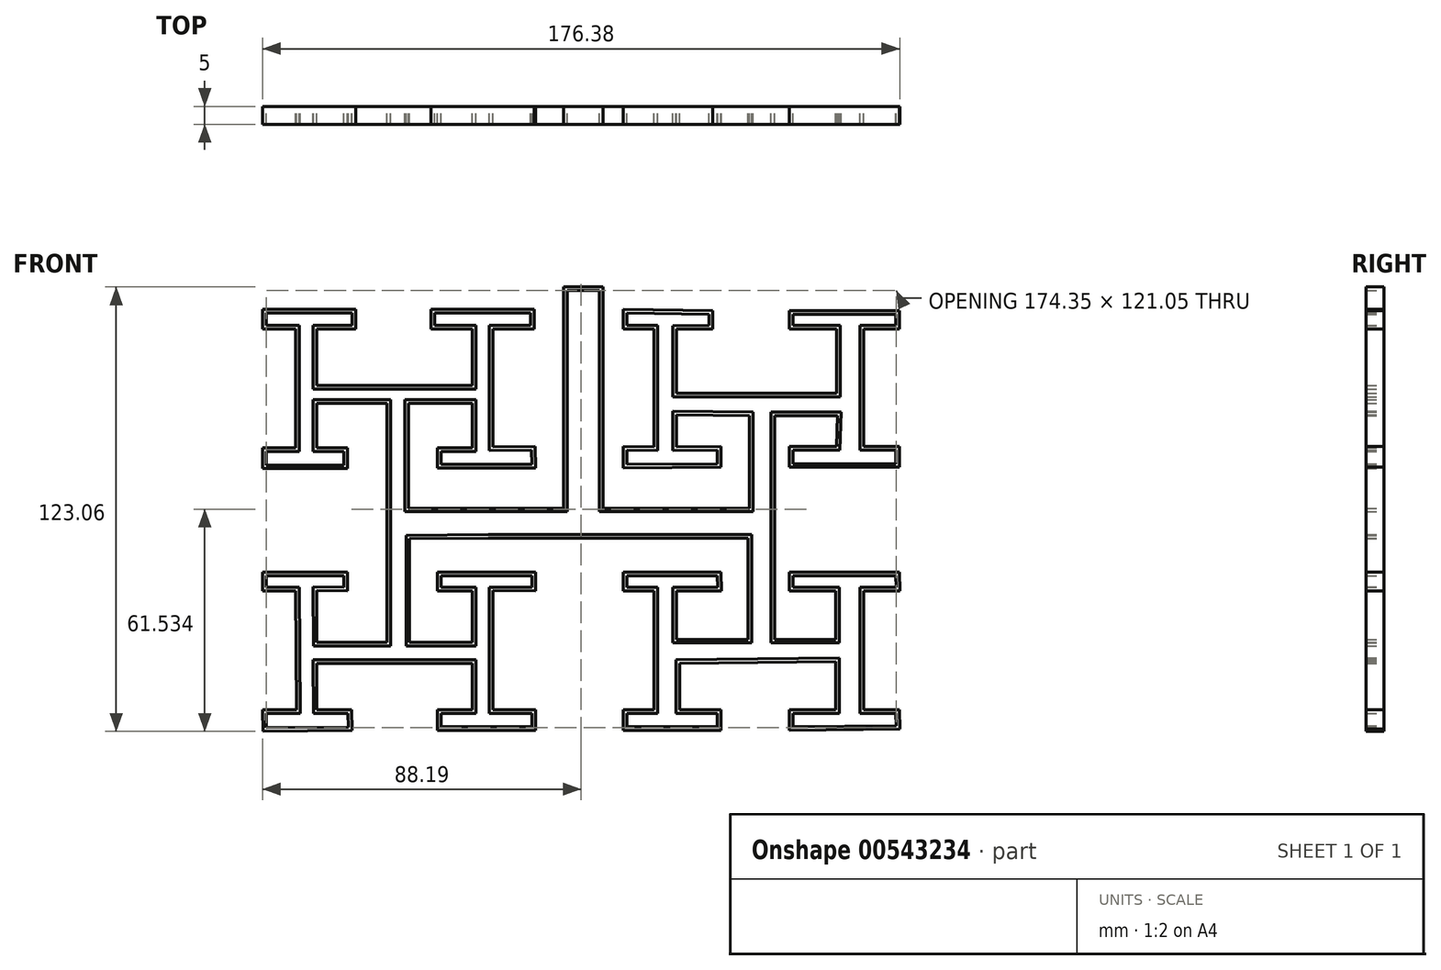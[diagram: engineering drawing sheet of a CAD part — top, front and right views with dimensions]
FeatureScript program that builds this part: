
annotation { "Feature Type Name" : "Feature", "Feature Type Description" : "" }
export const myFeature = defineFeature(function(context is Context, id is Id, definition is map)
    precondition{}
    {
        {
            var Q0;
            Q0=qCreatedBy(makeId("Front.planeOp"),FACE);
            var sketch = newSketch(context, id + "F0", { "sketchPlane" : qUnion([Q0])});
            skLineSegment(sketch, "E0", {"start": v(-2.88, 52.14) * mm, "end": v(-2.88, -9.1) * mm});
            skLineSegment(sketch, "E1", {"start": v(-2.88, -9.1) * mm, "end": v(-45.82, -9.1) * mm});
            skLineSegment(sketch, "E2", {"start": v(-45.82, -9.1) * mm, "end": v(-45.82, 19.95) * mm});
            skLineSegment(sketch, "E3", {"start": v(-45.82, 19.95) * mm, "end": v(-28.16, 19.92) * mm});
            skLineSegment(sketch, "E4", {"start": v(-28.16, 19.92) * mm, "end": v(-28.16, 7.64) * mm});
            skLineSegment(sketch, "E5", {"start": v(-28.16, 7.64) * mm, "end": v(-37.8, 7.64) * mm});
            skLineSegment(sketch, "E6", {"start": v(-37.8, 7.64) * mm, "end": v(-37.8, 2) * mm});
            skLineSegment(sketch, "E7", {"start": v(-22.51, 7.9) * mm, "end": v(-22.51, 40.51) * mm});
            skLineSegment(sketch, "E8", {"start": v(-28.12, 40.51) * mm, "end": v(-28.12, 24.82) * mm});
            skLineSegment(sketch, "E9", {"start": v(-51.83, 19.95) * mm, "end": v(-51.83, -46.23) * mm});
            skLineSegment(sketch, "E10", {"start": v(-23.69, -17.44) * mm, "end": v(48.1, -17.44) * mm});
            skLineSegment(sketch, "E11", {"start": v(48.1, -17.44) * mm, "end": v(48.1, -45.43) * mm});
            skLineSegment(sketch, "E12", {"start": v(55.47, -45.43) * mm, "end": v(55.47, 16.49) * mm});
            skLineSegment(sketch, "E13", {"start": v(55.47, 16.49) * mm, "end": v(72.86, 16.49) * mm});
            skLineSegment(sketch, "E14", {"start": v(72.6, 22.7) * mm, "end": v(28.32, 22.7) * mm});
            skLineSegment(sketch, "E15", {"start": v(28.32, 22.7) * mm, "end": v(28.32, 40.45) * mm});
            skLineSegment(sketch, "E16", {"start": v(22.09, 38.2) * mm, "end": v(22.09, 7.9) * mm});
            skLineSegment(sketch, "E17", {"start": v(28.32, 7.9) * mm, "end": v(28.32, 16.77) * mm});
            skLineSegment(sketch, "E18", {"start": v(28.32, 16.77) * mm, "end": v(48.48, 16.49) * mm});
            skLineSegment(sketch, "E19", {"start": v(48.48, 16.49) * mm, "end": v(48.48, -9.1) * mm});
            skLineSegment(sketch, "E20", {"start": v(48.48, -9.1) * mm, "end": v(8, -9.1) * mm});
            skLineSegment(sketch, "E21", {"start": v(8, -9.1) * mm, "end": v(8, 52.14) * mm});
            skLineSegment(sketch, "E22", {"start": v(8, 52.14) * mm, "end": v(-2.88, 52.14) * mm});
            skPoint(sketch, "E23", {"position": v(-45.53, -46.23) * mm});
            skLineSegment(sketch, "E24", {"start": v(-45.53, -46.23) * mm, "end": v(-45.53, -17.6) * mm});
            skLineSegment(sketch, "E25", {"start": v(-45.53, -17.6) * mm, "end": v(-23.69, -17.44) * mm});
            skLineSegment(sketch, "E26", {"start": v(-10.77, 7.97) * mm, "end": v(-10.7, 2.05) * mm});
            skLineSegment(sketch, "E27", {"start": v(-10.7, 2.05) * mm, "end": v(-37.8, 2) * mm});
            skLineSegment(sketch, "E28", {"start": v(55.47, -45.43) * mm, "end": v(55.47, -45.43) * mm});
            skLineSegment(sketch, "E29", {"start": v(48.1, -45.43) * mm, "end": v(28.32, -45.43) * mm});
            skLineSegment(sketch, "E30", {"start": v(28.32, -45.43) * mm, "end": v(28.32, -31.96) * mm});
            skLineSegment(sketch, "E31", {"start": v(55.47, -45.43) * mm, "end": v(72.44, -45.43) * mm});
            skLineSegment(sketch, "E32", {"start": v(72.44, -45.43) * mm, "end": v(72.44, -31.96) * mm});
            skLineSegment(sketch, "E33", {"start": v(80.19, -31.96) * mm, "end": v(80.19, -64.88) * mm});
            skLineSegment(sketch, "E34", {"start": v(72.44, -64.88) * mm, "end": v(72.44, -51.55) * mm});
            skLineSegment(sketch, "E35", {"start": v(72.44, -51.55) * mm, "end": v(29.26, -52.1) * mm});
            skLineSegment(sketch, "E36", {"start": v(29.26, -52.1) * mm, "end": v(29.26, -64.88) * mm});
            skLineSegment(sketch, "E37", {"start": v(22.09, -64.88) * mm, "end": v(22.09, -31.96) * mm});
            skLineSegment(sketch, "E38", {"start": v(72.6, 22.7) * mm, "end": v(72.6, 40.45) * mm});
            skLineSegment(sketch, "E39", {"start": v(80.19, 40.45) * mm, "end": v(80.19, 7.97) * mm});
            skLineSegment(sketch, "E40", {"start": v(72.6, 7.97) * mm, "end": v(72.86, 16.49) * mm});
            skLineSegment(sketch, "E41", {"start": v(-45.53, -46.23) * mm, "end": v(-28.16, -46.23) * mm});
            skLineSegment(sketch, "E42", {"start": v(-28.16, -46.23) * mm, "end": v(-28.16, -31.96) * mm});
            skLineSegment(sketch, "E43", {"start": v(-22.51, -31.95) * mm, "end": v(-22.51, -64.88) * mm});
            skLineSegment(sketch, "E44", {"start": v(-28.16, -64.88) * mm, "end": v(-28.16, -52.1) * mm});
            skLineSegment(sketch, "E45", {"start": v(-28.16, -52.1) * mm, "end": v(-71.21, -52.1) * mm});
            skLineSegment(sketch, "E46", {"start": v(-71.21, -52.1) * mm, "end": v(-71.19, -64.88) * mm});
            skLineSegment(sketch, "E47", {"start": v(-76.77, -64.88) * mm, "end": v(-77.1, -31.96) * mm});
            skLineSegment(sketch, "E48", {"start": v(-71.21, -31.85) * mm, "end": v(-71.19, -46.23) * mm});
            skLineSegment(sketch, "E49", {"start": v(-71.19, -46.23) * mm, "end": v(-51.83, -46.23) * mm});
            skLineSegment(sketch, "E50", {"start": v(-28.12, 24.82) * mm, "end": v(-71.21, 24.82) * mm});
            skLineSegment(sketch, "E51", {"start": v(-71.21, 24.82) * mm, "end": v(-71.21, 40.51) * mm});
            skLineSegment(sketch, "E52", {"start": v(-71.21, 19.95) * mm, "end": v(-51.83, 19.95) * mm});
            skLineSegment(sketch, "E53", {"start": v(-71.21, 19.95) * mm, "end": v(-71.21, 7.64) * mm});
            skLineSegment(sketch, "E54", {"start": v(-71.21, 7.64) * mm, "end": v(-62.8, 7.64) * mm});
            skLineSegment(sketch, "E55", {"start": v(-62.8, 7.64) * mm, "end": v(-62.8, 1.83) * mm});
            skLineSegment(sketch, "E56", {"start": v(-62.8, 1.83) * mm, "end": v(-86.2, 1.83) * mm});
            skLineSegment(sketch, "E57", {"start": v(-86.2, 1.83) * mm, "end": v(-86.2, 7.64) * mm});
            skLineSegment(sketch, "E58", {"start": v(-86.2, 7.64) * mm, "end": v(-77.1, 7.64) * mm});
            skLineSegment(sketch, "E59", {"start": v(-71.21, 40.51) * mm, "end": v(-60.44, 40.51) * mm});
            skLineSegment(sketch, "E60", {"start": v(-60.44, 40.51) * mm, "end": v(-60.44, 45.95) * mm});
            skLineSegment(sketch, "E61", {"start": v(-60.44, 45.95) * mm, "end": v(-86.2, 45.95) * mm});
            skLineSegment(sketch, "E62", {"start": v(-86.2, 40.51) * mm, "end": v(-77.1, 40.51) * mm});
            skLineSegment(sketch, "E63", {"start": v(-77.1, 40.51) * mm, "end": v(-77.1, 7.64) * mm});
            skLineSegment(sketch, "E64", {"start": v(-86.2, 45.95) * mm, "end": v(-86.2, 40.51) * mm});
            skLineSegment(sketch, "E65", {"start": v(-28.12, 40.51) * mm, "end": v(-39.55, 40.51) * mm});
            skLineSegment(sketch, "E66", {"start": v(-39.55, 40.51) * mm, "end": v(-39.55, 45.95) * mm});
            skLineSegment(sketch, "E67", {"start": v(-39.55, 45.95) * mm, "end": v(-11.1, 45.95) * mm});
            skLineSegment(sketch, "E68", {"start": v(-11.1, 45.95) * mm, "end": v(-11.1, 40.51) * mm});
            skLineSegment(sketch, "E69", {"start": v(-11.1, 40.51) * mm, "end": v(-22.51, 40.51) * mm});
            skLineSegment(sketch, "E70", {"start": v(-22.51, 7.9) * mm, "end": v(-10.77, 7.97) * mm});
            skLineSegment(sketch, "E71", {"start": v(-77.1, -31.96) * mm, "end": v(-86.2, -31.96) * mm});
            skLineSegment(sketch, "E72", {"start": v(-86.2, -31.96) * mm, "end": v(-86.26, -26.8) * mm});
            skLineSegment(sketch, "E73", {"start": v(-86.26, -26.8) * mm, "end": v(-62.8, -26.8) * mm});
            skLineSegment(sketch, "E74", {"start": v(-62.8, -26.8) * mm, "end": v(-62.74, -31.96) * mm});
            skLineSegment(sketch, "E75", {"start": v(-62.74, -31.96) * mm, "end": v(-71.21, -31.85) * mm});
            skLineSegment(sketch, "E76", {"start": v(-76.77, -64.88) * mm, "end": v(-86.2, -64.98) * mm});
            skLineSegment(sketch, "E77", {"start": v(-86.2, -64.98) * mm, "end": v(-86.14, -70.92) * mm});
            skLineSegment(sketch, "E78", {"start": v(-86.14, -70.92) * mm, "end": v(-61.5, -70.68) * mm});
            skPoint(sketch, "E78.endSnap0", {"position": v(-61.5, -46.23) * mm});
            skLineSegment(sketch, "E79", {"start": v(-61.5, -70.68) * mm, "end": v(-61.57, -64.88) * mm});
            skLineSegment(sketch, "E80", {"start": v(-61.57, -64.88) * mm, "end": v(-71.19, -64.88) * mm});
            skLineSegment(sketch, "E81", {"start": v(-28.16, -31.96) * mm, "end": v(-37.8, -31.96) * mm});
            skPoint(sketch, "E81.endSnap0", {"position": v(-37.8, 4.82) * mm});
            skLineSegment(sketch, "E82", {"start": v(-37.8, -31.96) * mm, "end": v(-37.8, -26.8) * mm});
            skLineSegment(sketch, "E83", {"start": v(-37.8, -26.8) * mm, "end": v(-10.7, -26.8) * mm});
            skLineSegment(sketch, "E84", {"start": v(-10.7, -26.8) * mm, "end": v(-10.67, -31.96) * mm});
            skLineSegment(sketch, "E85", {"start": v(-10.67, -31.96) * mm, "end": v(-22.51, -31.95) * mm});
            skLineSegment(sketch, "E86", {"start": v(-28.16, -64.88) * mm, "end": v(-37.8, -64.88) * mm});
            skLineSegment(sketch, "E87", {"start": v(-37.8, -64.88) * mm, "end": v(-37.8, -70.68) * mm});
            skLineSegment(sketch, "E88", {"start": v(-37.8, -70.68) * mm, "end": v(-10.67, -70.68) * mm});
            skLineSegment(sketch, "E89", {"start": v(-10.67, -70.68) * mm, "end": v(-10.67, -64.88) * mm});
            skLineSegment(sketch, "E90", {"start": v(-10.67, -64.88) * mm, "end": v(-22.51, -64.88) * mm});
            skLineSegment(sketch, "E91", {"start": v(22.09, -64.88) * mm, "end": v(13.55, -64.88) * mm});
            skLineSegment(sketch, "E92", {"start": v(13.55, -64.88) * mm, "end": v(13.55, -70.68) * mm});
            skLineSegment(sketch, "E93", {"start": v(13.55, -70.68) * mm, "end": v(40.66, -70.68) * mm});
            skLineSegment(sketch, "E94", {"start": v(40.66, -70.68) * mm, "end": v(40.66, -64.88) * mm});
            skLineSegment(sketch, "E95", {"start": v(40.66, -64.88) * mm, "end": v(29.26, -64.88) * mm});
            skLineSegment(sketch, "E96", {"start": v(72.44, -64.88) * mm, "end": v(59.64, -64.9) * mm});
            skLineSegment(sketch, "E97", {"start": v(59.64, -64.9) * mm, "end": v(59.64, -70.68) * mm});
            skLineSegment(sketch, "E98", {"start": v(59.64, -70.68) * mm, "end": v(90.12, -70.3) * mm});
            skLineSegment(sketch, "E99", {"start": v(90.12, -70.3) * mm, "end": v(90.05, -64.88) * mm});
            skLineSegment(sketch, "E100", {"start": v(90.05, -64.88) * mm, "end": v(80.19, -64.88) * mm});
            skLineSegment(sketch, "E101", {"start": v(22.09, -31.96) * mm, "end": v(13.55, -31.96) * mm});
            skLineSegment(sketch, "E102", {"start": v(13.55, -31.96) * mm, "end": v(13.55, -26.8) * mm});
            skLineSegment(sketch, "E103", {"start": v(13.55, -26.8) * mm, "end": v(40.66, -26.8) * mm});
            skLineSegment(sketch, "E104", {"start": v(40.66, -26.8) * mm, "end": v(40.73, -31.96) * mm});
            skLineSegment(sketch, "E105", {"start": v(40.73, -31.96) * mm, "end": v(28.32, -31.96) * mm});
            skLineSegment(sketch, "E106", {"start": v(72.44, -31.96) * mm, "end": v(59.64, -31.98) * mm});
            skLineSegment(sketch, "E107", {"start": v(59.64, -31.98) * mm, "end": v(59.64, -26.8) * mm});
            skLineSegment(sketch, "E108", {"start": v(59.64, -26.8) * mm, "end": v(90.05, -26.8) * mm});
            skLineSegment(sketch, "E109", {"start": v(90.05, -26.8) * mm, "end": v(90.11, -31.96) * mm});
            skLineSegment(sketch, "E110", {"start": v(90.11, -31.96) * mm, "end": v(80.19, -31.96) * mm});
            skLineSegment(sketch, "E111", {"start": v(22.09, 7.9) * mm, "end": v(13.55, 7.97) * mm});
            skLineSegment(sketch, "E112", {"start": v(13.55, 7.97) * mm, "end": v(13.55, 2.05) * mm});
            skLineSegment(sketch, "E113", {"start": v(13.55, 2.05) * mm, "end": v(40.66, 2.21) * mm});
            skLineSegment(sketch, "E114", {"start": v(40.66, 2.21) * mm, "end": v(40.63, 7.97) * mm});
            skLineSegment(sketch, "E115", {"start": v(40.63, 7.97) * mm, "end": v(28.32, 7.9) * mm});
            skLineSegment(sketch, "E116", {"start": v(22.09, 38.2) * mm, "end": v(22.09, 40.51) * mm});
            skLineSegment(sketch, "E117", {"start": v(22.09, 40.51) * mm, "end": v(13.55, 40.51) * mm});
            skLineSegment(sketch, "E118", {"start": v(13.55, 40.51) * mm, "end": v(13.55, 45.95) * mm});
            skLineSegment(sketch, "E119", {"start": v(13.55, 45.95) * mm, "end": v(38.4, 45.6) * mm});
            skPoint(sketch, "E119.endSnap0", {"position": v(38.4, 16.63) * mm});
            skLineSegment(sketch, "E120", {"start": v(38.4, 45.6) * mm, "end": v(38.4, 40.51) * mm});
            skLineSegment(sketch, "E121", {"start": v(38.4, 40.51) * mm, "end": v(28.32, 40.45) * mm});
            skLineSegment(sketch, "E122", {"start": v(72.6, 40.45) * mm, "end": v(59.64, 40.45) * mm});
            skLineSegment(sketch, "E123", {"start": v(59.64, 40.45) * mm, "end": v(59.64, 45.6) * mm});
            skLineSegment(sketch, "E124", {"start": v(59.64, 45.6) * mm, "end": v(90.05, 45.6) * mm});
            skLineSegment(sketch, "E125", {"start": v(90.05, 45.6) * mm, "end": v(90.05, 40.45) * mm});
            skLineSegment(sketch, "E126", {"start": v(90.05, 40.45) * mm, "end": v(80.19, 40.45) * mm});
            skLineSegment(sketch, "E127", {"start": v(72.6, 7.97) * mm, "end": v(59.64, 7.97) * mm});
            skLineSegment(sketch, "E128", {"start": v(59.64, 7.97) * mm, "end": v(59.64, 2.21) * mm});
            skLineSegment(sketch, "E129", {"start": v(59.64, 2.21) * mm, "end": v(90.05, 2.21) * mm});
            skLineSegment(sketch, "E130", {"start": v(90.05, 2.21) * mm, "end": v(90.05, 7.97) * mm});
            skLineSegment(sketch, "E131", {"start": v(90.05, 7.97) * mm, "end": v(80.19, 7.97) * mm});
            skSolve(sketch);
        }
        {
            var Q0;
            Q0 = qSketchRegion(id + "F0", true);
            extrude(context, id + "F1", {"entities" : qUnion([Q0]), "depth" : 5 * mm, "offsetDistance" : 25 * mm});
        }
        {
            var Q0;
            Q0=makeQuery(id+"F1.opExtrude","CAP_FACE",FACE,{"disambiguationData":[OSD([sQuery(id+"F0.wireOp",EDGE,"E0"),sQuery(id+"F0.wireOp",EDGE,"E1"),sQuery(id+"F0.wireOp",EDGE,"E2"),sQuery(id+"F0.wireOp",EDGE,"E3"),sQuery(id+"F0.wireOp",EDGE,"E4"),sQuery(id+"F0.wireOp",EDGE,"E5"),sQuery(id+"F0.wireOp",EDGE,"E6"),sQuery(id+"F0.wireOp",EDGE,"Uhj9fsSP-xh4G-2w61-e7PG-lvGmQOlik4t5"),sQuery(id+"F0.wireOp",EDGE,"E7"),sQuery(id+"F0.wireOp",EDGE,"oQomcRs6-VDuB-sYYi-fSPW-H2Tfd0qEHbaM"),sQuery(id+"F0.wireOp",EDGE,"UnowPzTY-xZr5-7Aet-b9ej-U1rt1Gu2egCq"),sQuery(id+"F0.wireOp",EDGE,"yyQZgFFz-2k0r-PoZb-v5ri-RnsavJP0LVhZ"),sQuery(id+"F0.wireOp",EDGE,"YYlCSO5O-rywH-7tDy-2e1c-VmEedtuGnNeI"),sQuery(id+"F0.wireOp",EDGE,"o7U1QUH9-Bizy-FnEP-bnXV-sUYex51NHFII"),sQuery(id+"F0.wireOp",EDGE,"3DAbgUuS-fvVc-geps-bFK8-xOxQtyu7GzQa"),sQuery(id+"F0.wireOp",EDGE,"E8"),sQuery(id+"F0.wireOp",EDGE,"IEaiaTz4-dMwO-VgY0-wrVl-V68zQjIATh8B"),sQuery(id+"F0.wireOp",EDGE,"E9"),sQuery(id+"F0.wireOp",EDGE,"E10"),sQuery(id+"F0.wireOp",EDGE,"E11"),sQuery(id+"F0.wireOp",EDGE,"4seGXC9S-5lUI-0MFB-faRe-gNnUsWFBkGLq"),sQuery(id+"F0.wireOp",EDGE,"E12"),sQuery(id+"F0.wireOp",EDGE,"E13"),sQuery(id+"F0.wireOp",EDGE,"ZPlPz8ge-dgCm-qWKU-5tTG-DJQ7y9RT0O0H"),sQuery(id+"F0.wireOp",EDGE,"E14"),sQuery(id+"F0.wireOp",EDGE,"E15"),sQuery(id+"F0.wireOp",EDGE,"3vezzqAC-wAgj-fnDP-g2lt-PDv5F4YDJ1Mo"),sQuery(id+"F0.wireOp",EDGE,"E16"),sQuery(id+"F0.wireOp",EDGE,"E17"),sQuery(id+"F0.wireOp",EDGE,"E18"),sQuery(id+"F0.wireOp",EDGE,"E19"),sQuery(id+"F0.wireOp",EDGE,"E20"),sQuery(id+"F0.wireOp",EDGE,"E21"),sQuery(id+"F0.wireOp",EDGE,"E22"),sQuery(id+"F0.wireOp",EDGE,"E24"),sQuery(id+"F0.wireOp",EDGE,"E25"),sQuery(id+"F0.wireOp",EDGE,"ETQssxLX-QlN4-Bsqe-sDEl-vYBZZVPnwrvs"),sQuery(id+"F0.wireOp",EDGE,"E26"),sQuery(id+"F0.wireOp",EDGE,"E27"),sQuery(id+"F0.wireOp",EDGE,"8nCNafXq-HolM-m2JL-76AW-AiOXpf6xnWZI"),sQuery(id+"F0.wireOp",EDGE,"e8pZc5By-Qqm5-OqoQ-K9ER-PWDTnBCWdlPG")])],"isStart":false});
            shell(context, id + "F2", {"entities" : qUnion([Q0]), "thickness" : 1 * mm});
        }
        {
            var Q0;
            Q0=makeQuery(id+"F2.opShell","OFFSET_FACE",FACE,{"disambiguationData":[OSD([sQuery(id+"F0.wireOp",EDGE,"E0"),sQuery(id+"F0.wireOp",EDGE,"E1"),sQuery(id+"F0.wireOp",EDGE,"E2"),sQuery(id+"F0.wireOp",EDGE,"E3"),sQuery(id+"F0.wireOp",EDGE,"E4"),sQuery(id+"F0.wireOp",EDGE,"E5"),sQuery(id+"F0.wireOp",EDGE,"E6"),sQuery(id+"F0.wireOp",EDGE,"E7"),sQuery(id+"F0.wireOp",EDGE,"E8"),sQuery(id+"F0.wireOp",EDGE,"E9"),sQuery(id+"F0.wireOp",EDGE,"E10"),sQuery(id+"F0.wireOp",EDGE,"E11"),sQuery(id+"F0.wireOp",EDGE,"E12"),sQuery(id+"F0.wireOp",EDGE,"E13"),sQuery(id+"F0.wireOp",EDGE,"E14"),sQuery(id+"F0.wireOp",EDGE,"E15"),sQuery(id+"F0.wireOp",EDGE,"E16"),sQuery(id+"F0.wireOp",EDGE,"E17"),sQuery(id+"F0.wireOp",EDGE,"E18"),sQuery(id+"F0.wireOp",EDGE,"E19"),sQuery(id+"F0.wireOp",EDGE,"E20"),sQuery(id+"F0.wireOp",EDGE,"E21"),sQuery(id+"F0.wireOp",EDGE,"E22"),sQuery(id+"F0.wireOp",EDGE,"E24"),sQuery(id+"F0.wireOp",EDGE,"E25"),sQuery(id+"F0.wireOp",EDGE,"E26"),sQuery(id+"F0.wireOp",EDGE,"E27"),sQuery(id+"F0.wireOp",EDGE,"E29"),sQuery(id+"F0.wireOp",EDGE,"E30"),sQuery(id+"F0.wireOp",EDGE,"E31"),sQuery(id+"F0.wireOp",EDGE,"E32"),sQuery(id+"F0.wireOp",EDGE,"E33"),sQuery(id+"F0.wireOp",EDGE,"E34"),sQuery(id+"F0.wireOp",EDGE,"E35"),sQuery(id+"F0.wireOp",EDGE,"E36"),sQuery(id+"F0.wireOp",EDGE,"E37"),sQuery(id+"F0.wireOp",EDGE,"E38"),sQuery(id+"F0.wireOp",EDGE,"E39"),sQuery(id+"F0.wireOp",EDGE,"E40"),sQuery(id+"F0.wireOp",EDGE,"E41"),sQuery(id+"F0.wireOp",EDGE,"E42"),sQuery(id+"F0.wireOp",EDGE,"E43"),sQuery(id+"F0.wireOp",EDGE,"E44"),sQuery(id+"F0.wireOp",EDGE,"E45"),sQuery(id+"F0.wireOp",EDGE,"E46"),sQuery(id+"F0.wireOp",EDGE,"E47"),sQuery(id+"F0.wireOp",EDGE,"E48"),sQuery(id+"F0.wireOp",EDGE,"E49"),sQuery(id+"F0.wireOp",EDGE,"E50"),sQuery(id+"F0.wireOp",EDGE,"E51"),sQuery(id+"F0.wireOp",EDGE,"E52"),sQuery(id+"F0.wireOp",EDGE,"E53"),sQuery(id+"F0.wireOp",EDGE,"E54"),sQuery(id+"F0.wireOp",EDGE,"E55"),sQuery(id+"F0.wireOp",EDGE,"E56"),sQuery(id+"F0.wireOp",EDGE,"E57"),sQuery(id+"F0.wireOp",EDGE,"E58"),sQuery(id+"F0.wireOp",EDGE,"E59"),sQuery(id+"F0.wireOp",EDGE,"E60"),sQuery(id+"F0.wireOp",EDGE,"E61"),sQuery(id+"F0.wireOp",EDGE,"E62"),sQuery(id+"F0.wireOp",EDGE,"E63"),sQuery(id+"F0.wireOp",EDGE,"E64"),sQuery(id+"F0.wireOp",EDGE,"E65"),sQuery(id+"F0.wireOp",EDGE,"E66"),sQuery(id+"F0.wireOp",EDGE,"E67"),sQuery(id+"F0.wireOp",EDGE,"E68"),sQuery(id+"F0.wireOp",EDGE,"E69"),sQuery(id+"F0.wireOp",EDGE,"E70"),sQuery(id+"F0.wireOp",EDGE,"E71"),sQuery(id+"F0.wireOp",EDGE,"E72"),sQuery(id+"F0.wireOp",EDGE,"E73"),sQuery(id+"F0.wireOp",EDGE,"E74"),sQuery(id+"F0.wireOp",EDGE,"E75"),sQuery(id+"F0.wireOp",EDGE,"E76"),sQuery(id+"F0.wireOp",EDGE,"E77"),sQuery(id+"F0.wireOp",EDGE,"E78"),sQuery(id+"F0.wireOp",EDGE,"E79"),sQuery(id+"F0.wireOp",EDGE,"E80"),sQuery(id+"F0.wireOp",EDGE,"E81"),sQuery(id+"F0.wireOp",EDGE,"E82"),sQuery(id+"F0.wireOp",EDGE,"E83"),sQuery(id+"F0.wireOp",EDGE,"E84"),sQuery(id+"F0.wireOp",EDGE,"E85"),sQuery(id+"F0.wireOp",EDGE,"E86"),sQuery(id+"F0.wireOp",EDGE,"E87"),sQuery(id+"F0.wireOp",EDGE,"E88"),sQuery(id+"F0.wireOp",EDGE,"E89"),sQuery(id+"F0.wireOp",EDGE,"E90"),sQuery(id+"F0.wireOp",EDGE,"E91"),sQuery(id+"F0.wireOp",EDGE,"E92"),sQuery(id+"F0.wireOp",EDGE,"E93"),sQuery(id+"F0.wireOp",EDGE,"E94"),sQuery(id+"F0.wireOp",EDGE,"E95"),sQuery(id+"F0.wireOp",EDGE,"E96"),sQuery(id+"F0.wireOp",EDGE,"E97"),sQuery(id+"F0.wireOp",EDGE,"E98"),sQuery(id+"F0.wireOp",EDGE,"E99"),sQuery(id+"F0.wireOp",EDGE,"E100"),sQuery(id+"F0.wireOp",EDGE,"E101"),sQuery(id+"F0.wireOp",EDGE,"E102"),sQuery(id+"F0.wireOp",EDGE,"E103"),sQuery(id+"F0.wireOp",EDGE,"E104"),sQuery(id+"F0.wireOp",EDGE,"E105"),sQuery(id+"F0.wireOp",EDGE,"E106"),sQuery(id+"F0.wireOp",EDGE,"E107"),sQuery(id+"F0.wireOp",EDGE,"E108"),sQuery(id+"F0.wireOp",EDGE,"E109"),sQuery(id+"F0.wireOp",EDGE,"E110"),sQuery(id+"F0.wireOp",EDGE,"E111"),sQuery(id+"F0.wireOp",EDGE,"E112"),sQuery(id+"F0.wireOp",EDGE,"E113"),sQuery(id+"F0.wireOp",EDGE,"E114"),sQuery(id+"F0.wireOp",EDGE,"E115"),sQuery(id+"F0.wireOp",EDGE,"E116"),sQuery(id+"F0.wireOp",EDGE,"E117"),sQuery(id+"F0.wireOp",EDGE,"E118"),sQuery(id+"F0.wireOp",EDGE,"E119"),sQuery(id+"F0.wireOp",EDGE,"E120"),sQuery(id+"F0.wireOp",EDGE,"E121"),sQuery(id+"F0.wireOp",EDGE,"E122"),sQuery(id+"F0.wireOp",EDGE,"E123"),sQuery(id+"F0.wireOp",EDGE,"E124"),sQuery(id+"F0.wireOp",EDGE,"E125"),sQuery(id+"F0.wireOp",EDGE,"E126"),sQuery(id+"F0.wireOp",EDGE,"E127"),sQuery(id+"F0.wireOp",EDGE,"E128"),sQuery(id+"F0.wireOp",EDGE,"E129"),sQuery(id+"F0.wireOp",EDGE,"E130"),sQuery(id+"F0.wireOp",EDGE,"E131")])]});
            extrude(context, id + "F3", {"entities" : qUnion([Q0]), "operationType" : NewBodyOperationType.REMOVE, "oppositeDirection" : true, "depth" : 25 * mm, "offsetDistance" : 25 * mm});
        }
    });
